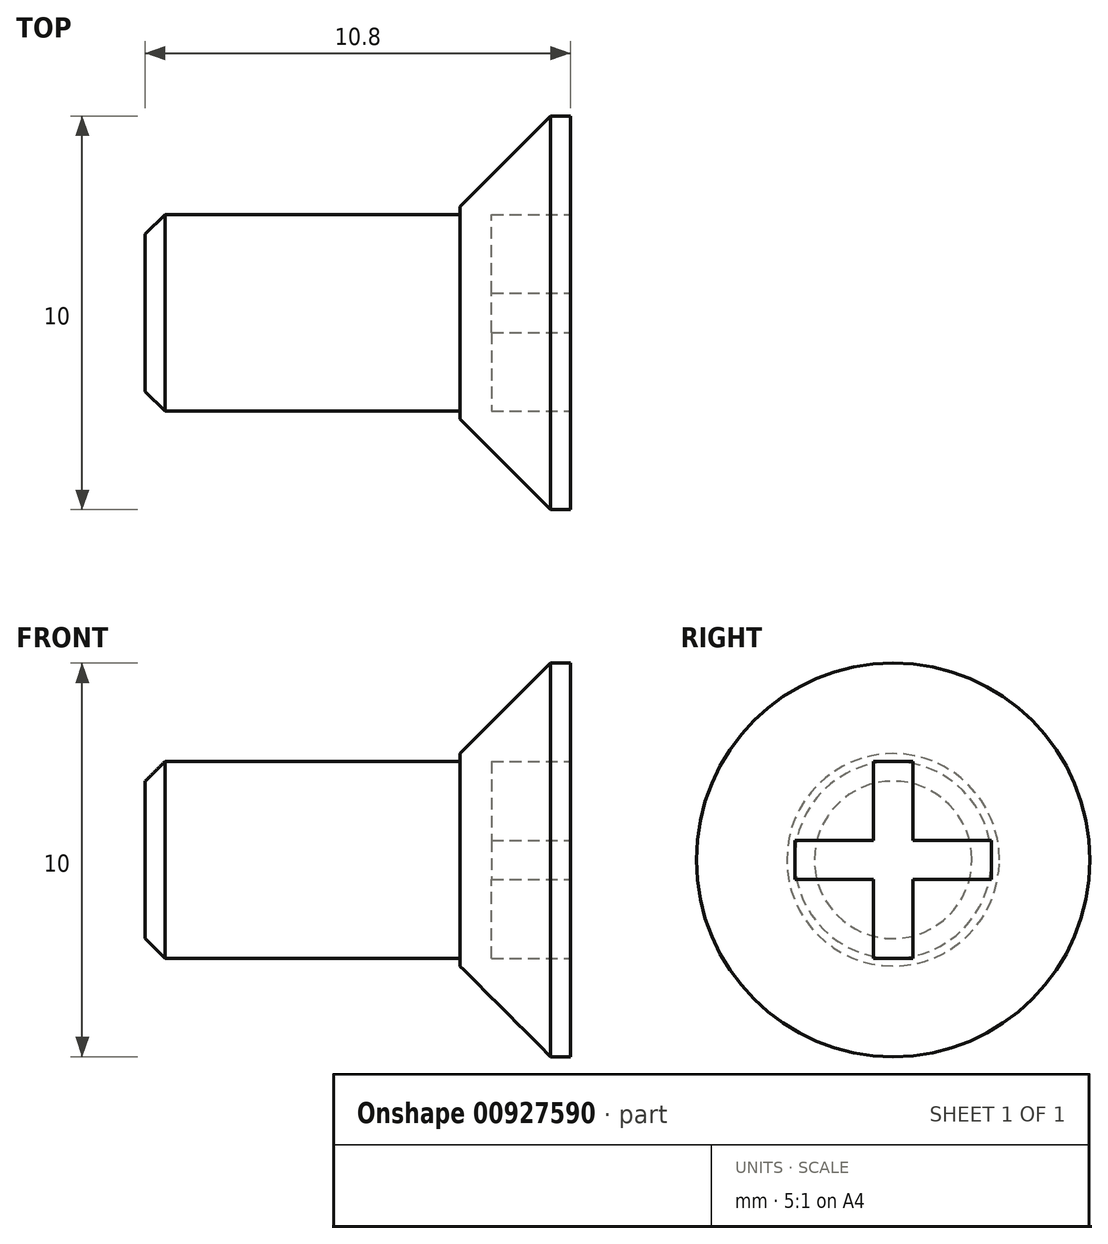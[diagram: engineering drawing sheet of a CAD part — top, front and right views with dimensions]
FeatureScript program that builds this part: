
annotation { "Feature Type Name" : "Feature", "Feature Type Description" : "" }
export const myFeature = defineFeature(function(context is Context, id is Id, definition is map)
    precondition{}
    {
        {
            var Q0;
            Q0=qCreatedBy(makeId("Right.planeOp"),FACE);
            var sketch = newSketch(context, id + "F0", { "sketchPlane" : qUnion([Q0])});
            skCircle(sketch, "E0", {"center": v(0, 0) * mm, "radius": 5 * mm});
            skSolve(sketch);
        }
        {
            var Q0;
            Q0 = qSketchRegion(id + "F0", true);
            extrude(context, id + "F1", {"entities" : qUnion([Q0]), "oppositeDirection" : true, "depth" : 2.8 * mm, "offsetDistance" : 25 * mm});
        }
        {
            var Q0;
            Q0=makeQuery(id+"F1.opExtrude","CAP_FACE",FACE,{"disambiguationData":[OSD([sQuery(id+"F0.wireOp",EDGE,"E0")])],"isStart":false});
            var sketch = newSketch(context, id + "F2", { "sketchPlane" : qUnion([Q0])});
            skCircle(sketch, "E1", {"center": v(0, 0) * mm, "radius": 2.5 * mm});
            skSolve(sketch);
        }
        {
            var Q0;
            Q0 = qSketchRegion(id + "F2", true);
            extrude(context, id + "F3", {"entities" : qUnion([Q0]), "operationType" : NewBodyOperationType.ADD, "depth" : 8 * mm, "offsetDistance" : 25 * mm});
        }
        {
            var Q0;
            Q0=makeQuery(id+"F1.opExtrude","CAP_EDGE",EDGE,{"disambiguationData":[OSD([sQuery(id+"F0.wireOp",EDGE,"E0")])],"isStart":false});
            chamfer(context, id + "F4", {"entities" : qUnion([Q0]), "width" : 2.3 * mm, "tangentPropagation" : true});
        }
        {
            var Q0;
            Q0=makeQuery(id+"F3.opExtrude","CAP_EDGE",EDGE,{"disambiguationData":[OSD([sQuery(id+"F2.wireOp",EDGE,"E1")])],"isStart":false});
            chamfer(context, id + "F5", {"entities" : qUnion([Q0]), "width" : 0.5 * mm, "tangentPropagation" : true});
        }
        {
            var Q0;
            Q0=makeQuery(id+"F1.opExtrude","CAP_FACE",FACE,{"disambiguationData":[OSD([sQuery(id+"F0.wireOp",EDGE,"E0")])],"isStart":true});
            var sketch = newSketch(context, id + "F6", { "sketchPlane" : qUnion([Q0])});
            skLineSegment(sketch, "E2", {"start": v(0, 3.86) * mm, "end": v(0, -3.3) * mm, "construction": true});
            skLineSegment(sketch, "E3", {"start": v(-4.57, 0) * mm, "end": v(5.84, 0) * mm, "construction": true});
            skLineSegment(sketch, "E4", {"start": v(0, 2.5) * mm, "end": v(0.5, 2.5) * mm});
            skLineSegment(sketch, "E5", {"start": v(0.5, 2.5) * mm, "end": v(0.5, 0.5) * mm});
            skLineSegment(sketch, "E6", {"start": v(0.5, 0.5) * mm, "end": v(2.5, 0.5) * mm});
            skLineSegment(sketch, "E7", {"start": v(2.5, 0.5) * mm, "end": v(2.5, 0) * mm});
            skLineSegment(sketch, "E8.MirrorCS", {"start": v(0, 2.5) * mm, "end": v(-0.5, 2.5) * mm});
            skLineSegment(sketch, "E9.MirrorCS", {"start": v(-0.5, 2.5) * mm, "end": v(-0.5, 0.5) * mm});
            skLineSegment(sketch, "E10.MirrorCS", {"start": v(-0.5, 0.5) * mm, "end": v(-2.5, 0.5) * mm});
            skLineSegment(sketch, "E11.MirrorCS", {"start": v(-2.5, 0.5) * mm, "end": v(-2.5, 0) * mm});
            skLineSegment(sketch, "E12.MirrorCS", {"start": v(0, -2.5) * mm, "end": v(0.5, -2.5) * mm});
            skLineSegment(sketch, "E13.MirrorCS", {"start": v(0, -2.5) * mm, "end": v(-0.5, -2.5) * mm});
            skLineSegment(sketch, "E14.MirrorCS", {"start": v(0.5, -2.5) * mm, "end": v(0.5, -0.5) * mm});
            skLineSegment(sketch, "E15.MirrorCS", {"start": v(-0.5, -2.5) * mm, "end": v(-0.5, -0.5) * mm});
            skLineSegment(sketch, "E16.MirrorCS", {"start": v(-0.5, -0.5) * mm, "end": v(-2.5, -0.5) * mm});
            skLineSegment(sketch, "E17.MirrorCS", {"start": v(0.5, -0.5) * mm, "end": v(2.5, -0.5) * mm});
            skLineSegment(sketch, "E18.MirrorCS", {"start": v(2.5, -0.5) * mm, "end": v(2.5, 0) * mm});
            skLineSegment(sketch, "E19.MirrorCS", {"start": v(-2.5, -0.5) * mm, "end": v(-2.5, 0) * mm});
            skSolve(sketch);
        }
        {
            var Q0;
            Q0 = qSketchRegion(id + "F6", true);
            extrude(context, id + "F7", {"entities" : qUnion([Q0]), "operationType" : NewBodyOperationType.REMOVE, "oppositeDirection" : true, "depth" : 2 * mm, "offsetDistance" : 25 * mm});
        }
    });
